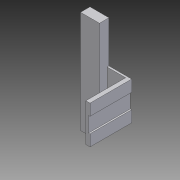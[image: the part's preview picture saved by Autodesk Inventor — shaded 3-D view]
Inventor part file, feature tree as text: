
AUTODESK INVENTOR PART (.ipt)
format: ipt  version: 2011 (Build 150239000, 239)  size: 93,696 bytes
history: native  units: in
note: dims shown in document units (in); Inventor stores cm internally (conversion verified against a paired STEP export)
features: other x1, imported_body x1, extrude x1, sketch x1
ambient origin geometry x8: Origin, YZ Plane, XZ Plane, XY Plane, X Axis, Y Axis, Z Axis, Center Point
feature tree (4):
  other  "Part2"
  imported_body  "Base1"
  extrude  "Extrusion1"  [1 undecoded]
  sketch  "Sketch1"  dims[d0=0.3937in d1=0.0in]
note: 1 required parameter value undecoded (feature->parameter linkage not recoverable at this tier; creation-order binding heuristic only, values carry confidence <= 0.55)
